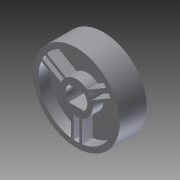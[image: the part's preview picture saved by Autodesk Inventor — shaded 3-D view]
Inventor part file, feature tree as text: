
AUTODESK INVENTOR PART (.ipt)
format: ipt  version: 2012 (Build 160160000, 160)  size: 173,056 bytes
history: native  units: in
note: dims shown in document units (in); Inventor stores cm internally (conversion verified against a paired STEP export)
features: extrude x2, sketch x1
ambient origin geometry x8: Origin, YZ Plane, XZ Plane, XY Plane, X Axis, Y Axis, Z Axis, Center Point
bodies: Solid1 (feature_tree)
feature tree (3):
  sketch  "Sketch1"  dims[d4=0.25in d5=0.3536in d6=0.3536in d7=0.75in d8=1.75in d9=2.0in d10=0.625in d11=0.0in d12=0.125in d13=0.0in d14=0.0625in d15=0.125in d16=0.0625in d17=0.0625in d18=30.0deg d19=1.1811in d21=360.0deg]
  extrude  "Extrusion1"  Depth=0.3536in
  extrude  "Extrusion2"  Depth=0.3536in
